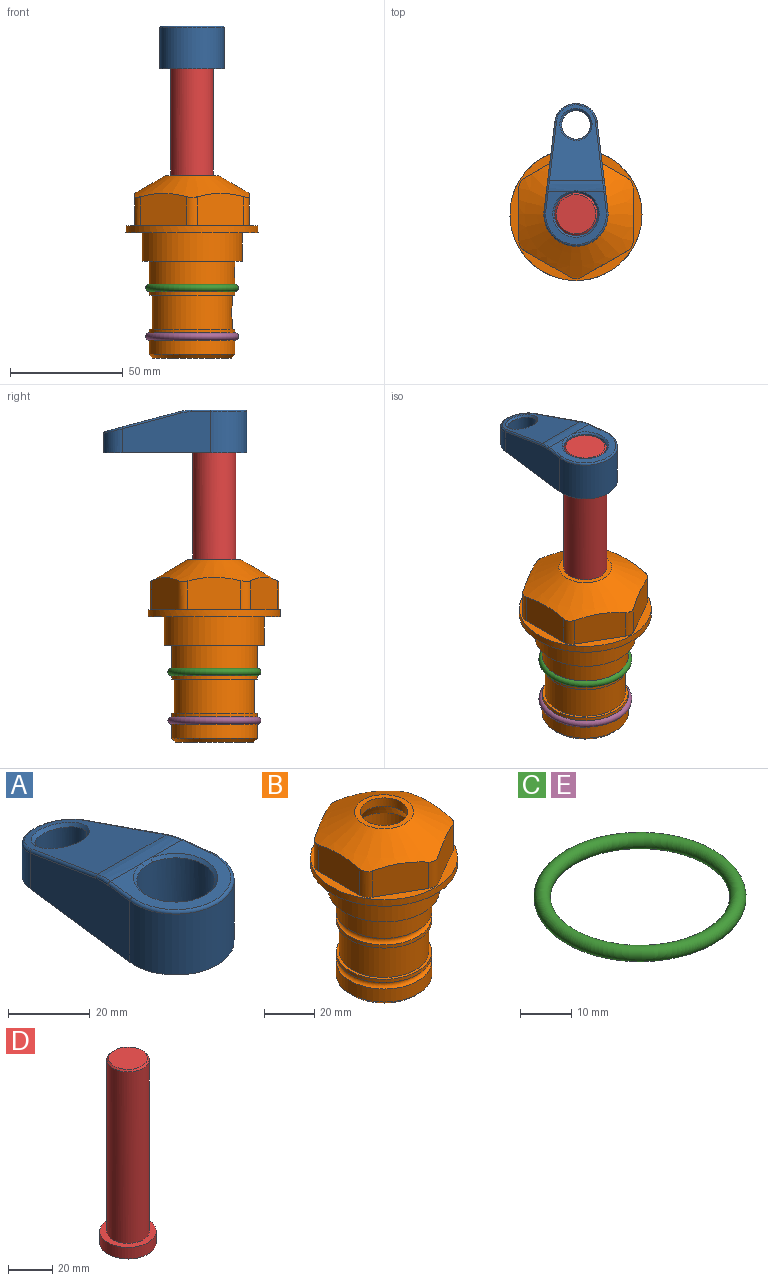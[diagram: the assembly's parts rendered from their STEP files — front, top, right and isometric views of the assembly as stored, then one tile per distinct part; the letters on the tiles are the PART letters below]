
ASSEMBLY  parts=5 mates=4
PART A: 31 faces, bbox 31.7x65.5x19.8 mm
  f0: plane 39.12x18.26mm, normal (0.99,0.12,0), area 612.2mm2, adj f1,f4,f7,f11,f13,f15
  f1: cylinder r=9.53mm len=18.91mm, axis (0,0,-1), area 296.1mm2, adj f0,f2,f7,f17
  f2: plane 39.12x18.26mm, normal (-0.99,0.12,0), area 612.2mm2, adj f1,f4,f7,f12,f14,f16
  f3: cylinder r=6.35mm len=12.7mm, axis (0,0,-1), area 362.4mm2, adj f7,f18
  f4: cylinder r=14.29mm len=28.58mm, axis (0,0,-1), area 882.2mm2, adj f0,f2,f7,f10
  f5: cylinder r=9.53mm len=19.05mm, axis (0,0,-1), area 1092.6mm2, adj f7,f19,f20
  f6: plane 26.99x23.69mm, normal (0,0,1), area 216.2mm2, adj f9,f10,f11,f12,f19
  f7: plane 63.5x28.58mm, normal (0,0,-1), area 661.8mm2, adj f0,f1,f2,f3,f4,f5,f22,f23
  f8: plane 33.52x23.6mm, normal (0,0.26,0.97), area 486mm2, adj f9,f15,f16,f17,f18
  f9: cylinder r=19.05mm len=24.72mm, axis (1,0,0), area 120.4mm2, adj f6,f8,f13,f14,f20
  f10: torus R=13.49mm, axis (0,0,1), area 59mm2, adj f4,f6,f11,f12
  f11: cylinder r=0.79mm len=8.67mm, axis (0.12,-0.99,0), area 10.8mm2, adj f0,f6,f10,f13
  f12: cylinder r=0.79mm len=8.67mm, axis (0.12,0.99,0), area 10.8mm2, adj f2,f6,f10,f14
  f13: bspline ~4.95x1.42mm, area 6.1mm2, adj f0,f9,f11,f15
  f14: bspline ~4.95x1.42mm, area 6.1mm2, adj f2,f9,f12,f16
  f15: cylinder r=0.79mm len=25.95mm, axis (0.12,-0.96,0.26), area 32.9mm2, adj f0,f8,f13,f17
  f16: cylinder r=0.79mm len=25.95mm, axis (0.12,0.96,-0.26), area 32.9mm2, adj f2,f8,f14,f17
  f17: bspline ~18.91x8.38mm, area 30mm2, adj f1,f8,f15,f16
  f18: bspline ~14.29x14.29mm, area 48.3mm2, adj f3,f8
  f19: cone r=9.53mm half-angle=45deg, axis (0,0,1), area 66.5mm2, adj f5,f6,f20
  f20: bspline ~3.22x0.96mm, area 3.5mm2, adj f5,f9,f19
  f21: plane 2.75x2.72mm, normal (0,0,-1), area 2.9mm2, adj f23,f25,f28
  f22: plane 23.05x15.88mm, normal (-0.99,-0.12,0), area 323.6mm2, adj f7,f25,f26,f27,f28,f29
  f23: plane 23.05x15.88mm, normal (0.99,-0.12,0), area 323.6mm2, adj f7,f21,f25,f27,f28,f30
  f24: cylinder r=9.53mm len=10.69mm, axis (0,0,-1), area 114.7mm2, adj f7,f27,f29,f30
  f25: cylinder r=12.7mm len=20.59mm, axis (0,0,-1), area 381.1mm2, adj f7,f21,f22,f23,f26,f28
  f26: plane 2.75x2.72mm, normal (0,0,-1), area 2.9mm2, adj f22,f25,f28
  f27: plane 19.72x18.37mm, normal (0,-0.26,-0.97), area 291.8mm2, adj f22,f23,f24,f28,f29,f30
  f28: cylinder r=15.88mm len=19.92mm, axis (1,0,0), area 54.8mm2, adj f21,f22,f23,f25,f26,f27
  f29: cylinder r=1.59mm len=11mm, axis (0,0,-1), area 34.7mm2, adj f7,f22,f24,f27
  f30: cylinder r=1.59mm len=11mm, axis (0,0,-1), area 34.7mm2, adj f7,f23,f24,f27
PART B: 36 faces, bbox 58.7x58.7x81 mm
  f0: cylinder r=17.78mm len=35.56mm, axis (0,0,1), area 1670.8mm2, adj f23,f24,f31
  f1: cylinder r=19.05mm len=38.1mm, axis (0,0,1), area 1191.9mm2, adj f26,f27,f30
  f2: plane 58.66x58.66mm, normal (0,0,-1), area 1150.6mm2, adj f3,f28
  f3: cylinder r=29.33mm len=58.66mm, axis (0,0,-1), area 585.1mm2, adj f2,f4
  f4: plane 58.66x58.66mm, normal (0,0,1), area 475.9mm2, adj f3,f5,f6,f7,f8,f9,f10,f11
  f5: plane 20.32x14.34mm, normal (-0.5,0.87,0), area 324.4mm2, adj f4,f15,f16,f17
  f6: plane 20.32x14.34mm, normal (0.5,0.87,0), area 324.4mm2, adj f4,f14,f15,f17
  f7: plane 23.48x14.34mm, normal (1,0,0), area 324.4mm2, adj f4,f13,f14,f17
  f8: plane 20.32x14.34mm, normal (0.5,-0.87,0), area 324.4mm2, adj f4,f12,f13,f17
  f9: plane 20.32x14.34mm, normal (-0.5,-0.87,0), area 324.4mm2, adj f4,f11,f12,f17
  f10: plane 23.48x14.34mm, normal (-1,0,0), area 324.4mm2, adj f4,f11,f16,f17
  f11: cylinder r=5.08mm len=12.85mm, axis (0,0,-1), area 67.2mm2, adj f4,f9,f10,f17
  f12: cylinder r=5.08mm len=12.85mm, axis (0,0,-1), area 67.2mm2, adj f4,f8,f9,f17
  f13: cylinder r=5.08mm len=12.85mm, axis (0,0,-1), area 67.2mm2, adj f4,f7,f8,f17
  f14: cylinder r=5.08mm len=12.85mm, axis (0,0,-1), area 67.2mm2, adj f4,f6,f7,f17
  f15: cylinder r=5.08mm len=12.85mm, axis (0,0,-1), area 67.2mm2, adj f4,f5,f6,f17
  f16: cylinder r=5.08mm len=12.85mm, axis (0,0,-1), area 67.2mm2, adj f4,f5,f10,f17
  f17: cone r=11.73mm half-angle=60deg, axis (0,0,-1), area 2071.8mm2, adj f5,f6,f7,f8,f9,f10,f11,f12
  f18: plane 23.46x23.46mm, normal (0,0,1), area 147.4mm2, adj f17,f35
  f19: plane 34.93x34.93mm, normal (0,0,-1), area 958mm2, adj f29
  f20: cylinder r=19.05mm len=38.1mm, axis (0,0,1), area 760.1mm2, adj f21,f29
  f21: torus R=19.05mm, axis (0,0,1), area 565.3mm2, adj f20,f22
  f22: cylinder r=19.05mm len=38.1mm, axis (0,0,1), area 190mm2, adj f21,f23
  f23: plane 38.1x38.1mm, normal (0,0,1), area 146.9mm2, adj f0,f22
  f24: plane 38.1x38.1mm, normal (0,0,-1), area 146.9mm2, adj f0,f25
  f25: cylinder r=19.05mm len=38.1mm, axis (0,0,1), area 190mm2, adj f24,f26
  f26: torus R=19.05mm, axis (0,0,1), area 565.3mm2, adj f1,f25
  f27: plane 44.45x44.45mm, normal (0,0,-1), area 411.7mm2, adj f1,f28
  f28: cylinder r=22.23mm len=44.45mm, axis (0,0,1), area 1773.5mm2, adj f2,f27
  f29: cone r=19.05mm half-angle=45deg, axis (0,0,1), area 257.5mm2, adj f19,f20
  f30: cylinder r=3.17mm len=6.75mm, axis (-1,0,0), area 128mm2, adj f1,f33
  f31: cylinder r=3.17mm len=6.35mm, axis (-1,0,0), area 102.5mm2, adj f0,f33
  f32: plane 25.4x25.4mm, normal (0,0,1), area 506.7mm2, adj f33
  f33: cylinder r=12.7mm len=66.42mm, axis (0,0,-1), area 5236.2mm2, adj f30,f31,f32,f34
  f34: cone r=9.53mm half-angle=30deg, axis (0,0,-1), area 443.4mm2, adj f33,f35
  f35: cylinder r=9.53mm len=19.05mm, axis (0,0,-1), area 240.9mm2, adj f18,f34
PART C: 1 faces, bbox 44.7x44.7x3.2 mm
  f0: torus R=19.05mm, axis (0,0,1), area 1193.9mm2
PART D: 6 faces, bbox 25.4x25.4x101.6 mm
  f0: plane 17.46x17.46mm, normal (0,0,1), area 239.5mm2, adj f5
  f1: plane 25.4x25.4mm, normal (0,0,-1), area 506.7mm2, adj f2
  f2: cylinder r=12.7mm len=25.4mm, axis (0,0,1), area 506.7mm2, adj f1,f3
  f3: plane 25.4x25.4mm, normal (0,0,1), area 221.7mm2, adj f2,f4
  f4: cylinder r=9.53mm len=94.46mm, axis (0,0,1), area 5653mm2, adj f3,f5
  f5: cone r=8.73mm half-angle=45deg, axis (0,0,-1), area 64.4mm2, adj f0,f4
PART E: same geometry as C
PLACE A t=(0,0,28.35)mm
PLACE B at identity fixed
PLACE C at identity
PLACE D t=(0,0,27.55)mm
PLACE E t=(0,0,-21.59)mm
MATE fastened E.f0 <-> B.f0  axis (0,0,1) through (0,0,-46.1)mm
MATE cylindrical D.f2 <-> B.f0  axis (0,0,-1) through (0,0,-10.55)mm
MATE fastened D.f2 <-> A.f4  axis (0,0,1) through (0,0,91.05)mm
MATE fastened C.f0 <-> B.f0  axis (0,0,1) through (0,0,-24.51)mm
